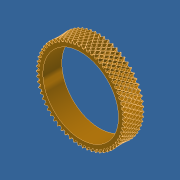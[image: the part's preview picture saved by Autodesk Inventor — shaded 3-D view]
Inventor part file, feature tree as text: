
AUTODESK INVENTOR PART (.ipt)
format: ipt  version: unknown  size: 4,575,232 bytes
history: native  units: in
note: dims shown in document units (in); Inventor stores cm internally (conversion verified against a paired STEP export)
features: sketch x5, loft x2, pattern_circular x2, extrude x1
ambient origin geometry x8: Origin, YZ Plane, XZ Plane, XY Plane, X Axis, Y Axis, Z Axis, Center Point
bodies: Solid1 (feature_tree)
feature tree (10):
  extrude  "Extrusion1"  Depth=1.0in TaperAngle=0.0deg
  loft  "Loft1"
  pattern_circular  "Circular Pattern1"  [2 undecoded]
  loft  "Loft3"
  pattern_circular  "Circular Pattern3"  [2 undecoded]
  sketch  "Sketch1"  dims[d0=4.0in d2=1.0in d3=0.0in]
  sketch  "Sketch2"  dims[d4=0.156in d5=0.12in]
  sketch  "Sketch3"  dims[d6=0.06in]
  sketch  "Sketch6"  dims[d8=0.673in]
  sketch  "Sketch7"  dims[d9=0.0in d10=0.156in d11=0.06in d12=0.06in d13=0.0in d14=90.0deg d15=0.0in d16=90.0deg d17=24.8031in d18=360.0deg d27=0.0in d28=90.0deg d29=0.0in d30=90.0deg d31=24.8031in d32=360.0deg d34=0.2in]
note: 4 required parameter values undecoded (feature->parameter linkage not recoverable at this tier; creation-order binding heuristic only, values carry confidence <= 0.55)
